# Revit family: MT-HB_BIFOLD DOOR_XXX
name_source: partatom
category: Doors
revit_build: Autodesk Revit 2017 (Build: 20160225_1515(x64)
units: mm (PartAtom-declared; Revit-internal decimal feet)

## family parameters
Always vertical = Yes
Cut with Voids When Loaded = No
Host = Wall
OmniClass Number = 23.30.20.00
OmniClass Title = Windows
Room Calculation Point = No
Shared = No

## types (2) — shared parameters
ANZRC COMPLIANT = YES
Analytic Construction = <None>
DOUBLE GLAZED THICKNESS = 18 mm  [stored 0.0590551 ft]
FRAME MATERIAL = <By Category>
GLAZED MATERIAL = Glass
Height = 2100 mm
MAX HEIGHT = 3000 mm  [stored 9.84252 ft]
MAX PANEL HEIGHT = 3000 mm  [stored 9.84252 ft]
MAX PANEL WIDTH = 1000 mm  [stored 3.28084 ft]
MAX WIDTH = 3000 mm  [stored 9.84252 ft]
Manufacturer = ALSPEC
Model = HAWKESBURY TOP HUNG COMMERCIAL MULTI-FOLD DOOR
OFFSET = 10 mm  [stored 0.0328084 ft]
OVERALL FRAME HEIGHT = 2100 mm
Rough Height = 2100 mm
SINGLE GLAZED THICKNESS = 5 mm  [stored 0.0164042 ft]
URL = WWW.ALSPEC.COM.AU
VERSION = 2.1
WARNING = No
Wall Closure = By host
YEAR = 2019
zero-valued in all types: Default Sill Height, TOLERANCE

## per-type parameters (varying)
| type | 101.6mm FRAME THICKNESS | 150mm FRAME THICKNESS | 2L1R/1L2R | 3L/3R | A | AIR POCKET | BOT PANEL POSITION | DETAIL_DEPTH SILL | DOUBLE GLAZED | FRAME THICKNESS | OVERALL FRAME WIDTH | PANEL HEIGHT | PANEL WIDTH | Rough Width | TOP PANEL POSITION | Width |
| 2L1R/1L2R | No | Yes | Yes | No | 4 mm  [stored 0.0131234 ft] | 8 mm  [stored 0.0262467 ft] | 95 mm | 150 mm | No | 76 mm  [stored 0.249344 ft] | 1500 mm  [stored 4.92126 ft] | 1907 mm | 464 mm  [stored 1.52231 ft] | 1500 mm  [stored 4.92126 ft] | 1891 mm | 1500 mm  [stored 4.92126 ft] |
| 1L1R | Yes | No | No | Yes | 40 mm  [stored 0.131234 ft] | 5 mm  [stored 0.0164042 ft] | 35 mm | 102 mm | Yes | 102 mm | 2000 mm  [stored 6.56168 ft] | 1982 mm | 630 mm | 2000 mm  [stored 6.56168 ft] | 1966 mm | 2000 mm  [stored 6.56168 ft] |

note: [stored X ft] marks values corroborated as IEEE doubles in the binary element streams (Revit-internal decimal feet)

## geometry (parser evidence)
native form markers: Extrusion x1, Sweep x32
no freeform markers — native parametric forms only
